# Revit family: Haworth_Epure_120DegreeDesk_AP_PRELIMINARY
name_source: partatom
category: Furniture
units: mm (PartAtom-declared; Revit-internal decimal feet)

## family parameters
Always vertical = Yes
Cut with Voids When Loaded = No
OmniClass Number = 23.40.70.14.64.11
OmniClass Title = Office Furniture
Room Calculation Point = No
Shared = No
Work Plane-Based = No

## types (3) — shared parameters
Actual Height = 730 mm  [stored 2.39501 ft]
Actual Width = 1400 mm  [stored 4.59318 ft]
Assembly Code = E2020200
Cable Tray Finish = Haworth _ Polymer _ Undecided
Depth = 700 mm  [stored 2.29659 ft]
Description = Haworth - Epure -120 Degree Desk
Flip Top Finish = Haworth _ Paint _ Metallic Silver
Large Aluminium = No
Leg Height = 695 mm  [stored 2.28018 ft]
Manufacturer = Haworth
Medium Wood = No
Model = SYEP12D1X0X1X0X
Revision Number = 1
Size = Verify Final Dim.w/ Haworth
Small Wood = No
Trim Finish = Haworth _ Metal _ Structured White EC
URL = https://www.haworth.com
URL - Product = https://www.haworth.com
Warranty = http://www.haworth.com
Worksurface Dimension = 1200/700 x 1200/700, 1400/700 x 800/700, 1400/700 x 1400/700 mm

## per-type parameters (varying)
| type | Accessory Kit | Actual Depth | Aluminium Legs | Cable Tray | Cable Tray Width | Flip Top Cable Outlet | Large | Large Wood | Leg Width | Medium | Medium Aluminium | No Accessory Kit | Round Cable Outlet | Small | Small Aluminium | Umbilical Cord | Wooden Legs |
| 1200/700 x 1200/700 | No | 800 mm  [stored 2.62467 ft] | Yes | No | 700 mm  [stored 2.29659 ft] | No | No | No | 200 mm | No | No | Yes | No | Yes | Yes | No | No |
| 1400/700 x 1400/700 | Yes | 1400 mm  [stored 4.59318 ft] | No | Yes | 850 mm | Yes | Yes | Yes | 50 mm | No | No | No | No | No | No | Yes | Yes |
| 1400/700 x 800/700 | Yes | 800 mm  [stored 2.62467 ft] | Yes | Yes | 800 mm  [stored 2.62467 ft] | No | No | No | 80 mm  [stored 0.262467 ft] | Yes | Yes | No | Yes | No | No | Yes | No |

type visibility flags: 3 boolean params named "<type name>" — each type sets only its own to Yes (folded from table)

note: [stored X ft] marks values corroborated as IEEE doubles in the binary element streams (Revit-internal decimal feet)

## geometry (parser evidence)
native form markers: Sweep x25
no freeform markers — native parametric forms only
